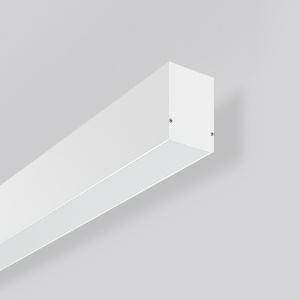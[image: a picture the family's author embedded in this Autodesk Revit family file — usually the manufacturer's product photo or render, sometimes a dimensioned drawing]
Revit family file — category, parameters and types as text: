
# Revit family: less_is_more_50_312609_002_1_80da
name_source: partatom
category: Lighting Fixtures
units: mm (PartAtom-declared; Revit-internal decimal feet)

## family parameters
Cut with Voids When Loaded = No
Host = Face
Light Source = No
Part Type = Normal
Room Calculation Point = No
Round Connector Dimension = Use Diameter
Shared = No

## types (1)
- LESS IS MORE 50 (1 x LED Modul 840, 1950 lm, 4000)
    Apparent Load = 15 VA
    CIE Flux Codes = 48 80 96 100 100
    Color Rendering = 80
    Color Temperature = 4000
    Default Elevation = 1800 mm
    Description = Series: LESS IS MORE 50
Linear wall luminaires. Housing: extruded aluminium profile, powder-coated. End cap aluminium powder-coated. Diffuser made of non-yellowing plastic (PMMA), opal. Direct light emission. Suitable for Wall (surface). LED unit with integrated converter interchangeable and removable. Suitable for through-wiring. With sensors or as a safety luminaire on request. 
Colour: traffic white, matt (RAL 9016)
Length: 1407 mm
Width: 67 mm
Height: 75 mm
Lamp: LED
Socket: without socket
Colour temperature: 4000K
Colour rendering index (CRI): 80
System power: 15 W
Rated luminous flux: 1950 lm
Luminous efficiency: 130 lm/W
Control gear: Regulated power supply
Protection class: I
Type of protection: IP 20
    Height = 75 mm
    Lamp = 1 x LED Modul 840
    Lamp Light Flux = 1950 lm
    Lamp count = 1
    Length = 1407 mm
    Lifetime = 50000 h
    Luminous efficacy = 130 lm/W
    Manufacturer = RZB
    ModVariant = No
    Model = 312609.002.1
    Mounting Place = Wall
    Mounting Type = Surface mounted
    Number of Poles = 1
    OnlyDefault = Yes
    Power Factor = 1
    Product Name = LESS IS MORE 50
    Product group = Surface mounted LED linear luminaires
    ProductGroupID = 2007
    Protection Class = Protection class I
    Protection Degree = IP 20
    RLX_Detail_Level = 1
    RLX_Emergency_Light_Flux = 0 lm
    RLX_Emergency_Type = 0
    RLX_Emergency_Type_DB = No
    RlxData = <blob elided: 35185 chars, md5=1e5b6856>
    Socket = socket
    Standby Power = 0 W
    System Light Flux = 1950 lm
    System Power = 15 W
    Type Comments = Product without accessories
    Type Image = 312606.002.jpg
    URL = http://relux.com
    VarID = ---
    Voltage = 0 V
    Weight = 0.00 kg
    Width = 67 mm

## geometry (parser evidence)
native form markers: Blend x4, Sweep x12
no freeform markers — native parametric forms only
